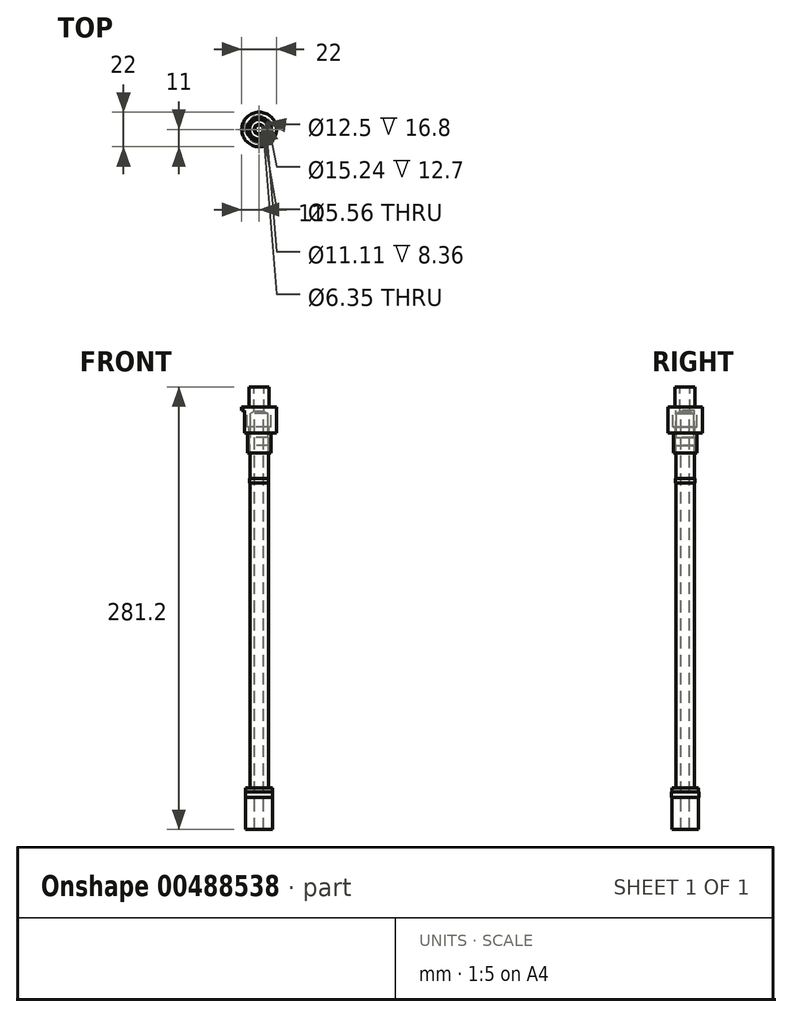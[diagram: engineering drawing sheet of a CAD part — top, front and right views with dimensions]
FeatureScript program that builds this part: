
annotation { "Feature Type Name" : "Feature", "Feature Type Description" : "" }
export const myFeature = defineFeature(function(context is Context, id is Id, definition is map)
    precondition{}
    {
        {
            var Q0;
            Q0=qCreatedBy(makeId("Front.planeOp"),FACE);
            var sketch = newSketch(context, id + "F0", { "sketchPlane" : qUnion([Q0])});
            skLineSegment(sketch, "E0", {"start": v(0, 0) * mm, "end": v(-8.5, 0) * mm});
            skLineSegment(sketch, "E1", {"start": v(-8.5, 0) * mm, "end": v(-8.5, 20.5) * mm});
            skLineSegment(sketch, "E2", {"start": v(-8.5, 20.5) * mm, "end": v(-8.65, 20.5) * mm});
            skLineSegment(sketch, "E3", {"start": v(-8.65, 20.5) * mm, "end": v(-8.65, 24) * mm});
            skLineSegment(sketch, "E4", {"start": v(-8.65, 24) * mm, "end": v(-8.5, 24) * mm});
            skLineSegment(sketch, "E5", {"start": v(-8.5, 24) * mm, "end": v(-8.5, 26.5) * mm});
            skLineSegment(sketch, "E6", {"start": v(-8.5, 26.5) * mm, "end": v(-5.88, 26.5) * mm});
            skLineSegment(sketch, "E7", {"start": v(-5.87, 26.5) * mm, "end": v(-5.88, 220) * mm});
            skLineSegment(sketch, "E8", {"start": v(-5.88, 220) * mm, "end": v(-6.1, 220) * mm});
            skLineSegment(sketch, "E9", {"start": v(-6.1, 220) * mm, "end": v(-6.1, 223) * mm});
            skLineSegment(sketch, "E10", {"start": v(-6.1, 223) * mm, "end": v(-5.88, 223) * mm});
            skLineSegment(sketch, "E11", {"start": v(-5.88, 223) * mm, "end": v(-5.88, 244) * mm});
            skLineSegment(sketch, "E12", {"start": v(-5.88, 244) * mm, "end": v(-6.1, 244) * mm});
            skLineSegment(sketch, "E13", {"start": v(-6.1, 244) * mm, "end": v(-6.1, 249) * mm});
            skLineSegment(sketch, "E14", {"start": v(0, 264.16) * mm, "end": v(0, 0) * mm});
            skLineSegment(sketch, "E15", {"start": v(-5.56, 249) * mm, "end": v(-5.56, 264.16) * mm});
            skLineSegment(sketch, "E16", {"start": v(-2.78, 264.16) * mm, "end": v(-2.78, 0) * mm});
            skLineSegment(sketch, "E17", {"start": v(0, 264.16) * mm, "end": v(-5.56, 264.16) * mm});
            skLineSegment(sketch, "E18", {"start": v(-5.56, 249) * mm, "end": v(-6.1, 249) * mm});
            skSolve(sketch);
        }
        {
            var Q0;
            {var subQ0=sQuery(id+"F0.wireOp",EDGE,"E1");Q0=makeQuery(id+"F0.imprint","IMPRINT",FACE,{"disambiguationData":[TD([[makeQuery(id+"F0.imprint","IMPRINT",EDGE,{"derivedFrom":subQ0}),-1.0]])]});}
            var Q1;
            Q1=sQuery(id+"F0.wireOp",EDGE,"E14");
            revolve(context, id + "F1", {"entities" : qUnion([Q0]), "axis" : qUnion([Q1]), "revolveType" : RevolveType.FULL});
        }
        {
            var Q0;
            Q0=qCreatedBy(makeId("Front.planeOp"),FACE);
            var sketch = newSketch(context, id + "F2", { "sketchPlane" : qUnion([Q0])});
            skLineSegment(sketch, "E19", {"start": v(0, 239) * mm, "end": v(-7.5, 239) * mm});
            skLineSegment(sketch, "E20", {"start": v(-7.5, 239) * mm, "end": v(-7.5, 252) * mm});
            skLineSegment(sketch, "E21", {"start": v(-7.5, 252) * mm, "end": v(-11, 252) * mm});
            skLineSegment(sketch, "E22", {"start": v(-11, 252) * mm, "end": v(-11, 268.5) * mm});
            skLineSegment(sketch, "E23", {"start": v(-11, 268.5) * mm, "end": v(0, 268.5) * mm});
            skLineSegment(sketch, "E24", {"start": v(0, 268.5) * mm, "end": v(0, 239) * mm});
            skLineSegment(sketch, "E25", {"start": v(-9.37, 252) * mm, "end": v(-9.37, 266) * mm});
            skLineSegment(sketch, "E26", {"start": v(-9.37, 266) * mm, "end": v(-11, 266) * mm});
            skLineSegment(sketch, "E27", {"start": v(-6.25, 268.5) * mm, "end": v(-6.25, 239) * mm});
            skLineSegment(sketch, "E28", {"start": v(-7.62, 268.5) * mm, "end": v(-7.62, 255.8) * mm});
            skLineSegment(sketch, "E29", {"start": v(-7.62, 255.8) * mm, "end": v(-6.25, 255.8) * mm});
            skSolve(sketch);
        }
        {
            var Q0;
            {var subQ3=sQuery(id+"F2.wireOp",EDGE,"E25");Q0=makeQuery(id+"F2.imprint","IMPRINT",FACE,{"disambiguationData":[TD([[makeQuery(id+"F2.imprint","IMPRINT",EDGE,{"derivedFrom":subQ3}),1.0]])]});}
            var Q1;
            {var subQ4=sQuery(id+"F2.wireOp",EDGE,"E20");Q1=makeQuery(id+"F2.imprint","IMPRINT",FACE,{"disambiguationData":[TD([[makeQuery(id+"F2.imprint","IMPRINT",EDGE,{"derivedFrom":subQ4}),-1.0]])]});}
            var Q2;
            Q2=sQuery(id+"F2.wireOp",EDGE,"E24");
            revolve(context, id + "F3", {"entities" : qUnion([Q0, Q1]), "axis" : qUnion([Q2]), "revolveType" : RevolveType.FULL});
        }
        {
            var Q0;
            {var subQ3=sQuery(id+"F2.wireOp",EDGE,"E25");Q0=makeQuery(id+"F2.imprint","IMPRINT",FACE,{"disambiguationData":[TD([[makeQuery(id+"F2.imprint","IMPRINT",EDGE,{"derivedFrom":subQ3}),1.0]])]});}
            extrude(context, id + "F4", {"entities" : qUnion([Q0]), "operationType" : NewBodyOperationType.REMOVE, "oppositeDirection" : true, "depth" : 25.4 * mm, "symmetric" : true});
        }
        {
            var Q0;
            Q0=qCreatedBy(makeId("Front.planeOp"),FACE);
            var sketch = newSketch(context, id + "F5", { "sketchPlane" : qUnion([Q0])});
            skLineSegment(sketch, "E30", {"start": v(0, 255.8) * mm, "end": v(-7.62, 255.8) * mm});
            skLineSegment(sketch, "E31", {"start": v(-7.62, 255.8) * mm, "end": v(-7.62, 268.5) * mm});
            skLineSegment(sketch, "E32", {"start": v(-7.62, 268.5) * mm, "end": v(-6.35, 268.5) * mm});
            skLineSegment(sketch, "E33", {"start": v(-6.35, 268.5) * mm, "end": v(-6.35, 281.2) * mm});
            skLineSegment(sketch, "E34", {"start": v(-6.35, 281.2) * mm, "end": v(0, 281.2) * mm});
            skLineSegment(sketch, "E35", {"start": v(0, 281.2) * mm, "end": v(0, 255.8) * mm});
            skLineSegment(sketch, "E36", {"start": v(-5.56, 255.8) * mm, "end": v(-5.56, 264.16) * mm});
            skLineSegment(sketch, "E37", {"start": v(-5.56, 264.16) * mm, "end": v(0, 264.16) * mm});
            skLineSegment(sketch, "E38", {"start": v(-3.18, 281.2) * mm, "end": v(-3.17, 264.16) * mm});
            skLineSegment(sketch, "E39", {"start": v(-5.56, 264.16) * mm, "end": v(-3.17, 265.6) * mm});
            skSolve(sketch);
        }
        {
            var Q0;
            {var subQ1=sQuery(id+"F5.wireOp",EDGE,"E31");Q0=makeQuery(id+"F5.imprint","IMPRINT",FACE,{"disambiguationData":[TD([[makeQuery(id+"F5.imprint","IMPRINT",EDGE,{"derivedFrom":subQ1}),-1.0]])]});}
            var Q1;
            Q1=sQuery(id+"F5.wireOp",EDGE,"E35");
            revolve(context, id + "F6", {"entities" : qUnion([Q0]), "axis" : qUnion([Q1]), "revolveType" : RevolveType.FULL});
        }
    });
